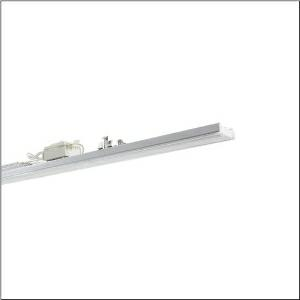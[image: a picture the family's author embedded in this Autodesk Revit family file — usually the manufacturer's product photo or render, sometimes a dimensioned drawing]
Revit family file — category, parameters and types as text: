
# Revit family: licross_r__11_recessed_mo_51tl12dn49xg_9b29
name_source: partatom
category: Lighting Fixtures
units: mm (PartAtom-declared; Revit-internal decimal feet)

## family parameters
Cut with Voids When Loaded = No
Host = Face
Light Source = No
Part Type = Normal
Room Calculation Point = No
Round Connector Dimension = Use Diameter
Shared = No

## types (1)
- --- (1 x LED, 9140 lm, 50.1 W, 4000K)
    Apparent Load = 50 VA
    CIE Flux Codes = 67 92 99 100 100
    Color Rendering = 80
    Color Temperature = 4000K
    Default Elevation = 1800 mm
    Description = Licross® 11 Recessed MO, luminaire insert, of sheet steel, coil coated, white, length: 1.500mm, width: 66mm, height: 67mm, LED rated luminous flux: 9.140lm, light colour: 840, control gear: DALI 2, with plug, 5-pole, with phase selection, mains connection: 220..240V, AC, 50/60Hz, rated input power: 50W, internal wiring halogen-free, primary optical cover: cover, of PMMA, light emission: direct distribution, primary light characteristic: symmetric, protection rating (complete): IP40, insulation class (complete): insulation class I (protective earthing), certification: CE, ENEC, VDE, UKCA, protection symbol: D if used in an environment without relevant dust loads with corresponding accessories, impact resistance: IK06, permissible ambient temperature for indoor applications: -25..+35°C, corresponds to IFS (International Featured Standards) requirements for safety and quality in the food industry, reducing of maximum allowable ambient temperature of 5°C with ceiling mounting, LABS conformity tested according to VDMA 24364:2018-05, packaging unit: 1 piece
    Height = 58 mm
    Lamp = 1 x LED
    Lamp Light Flux = 9140 lm
    Lamp Power = 50.1 W
    Lamp count = 1
    Length = 1500 mm
    Luminous efficacy = 182 lm/W
    Manufacturer = Siteco
    ModVariant = No
    Model = 51TL12DN49XG
    Mounting Place = Ceiling
    Mounting Type = Pendant
    Number of Poles = 1
    OnlyDefault = Yes
    Power Factor = 1
    Product Name = Licross® 11 Recessed MO
    Product group = luminaire insert | ceiling pendant
    ProductGroupID = 902
    Protection Class = Protection class I
    Protection Degree = IP 40
    RLX_Detail_Level = 1
    RLX_Emergency_Light_Flux = 0 lm
    RLX_Emergency_Type = 0
    RLX_Emergency_Type_DB = No
    RlxData = <blob elided: 24509 chars, md5=cb95525c>
    Socket = socket
    Standby Power = 0 W
    System Light Flux = 9140 lm
    System Power = 50 W
    Type Comments = factory setting: luminous flux: 100 % | dim-lin: 254 | 334 mA
    Type Image = l_1296930.jpg
    URL = http://relux.com
    VarID = @adj_029135
    Voltage = 0 V
    Weight = 0.00 kg
    Width = 66 mm

## geometry (parser evidence)
native form markers: Blend x4, Sweep x13
no freeform markers — native parametric forms only
